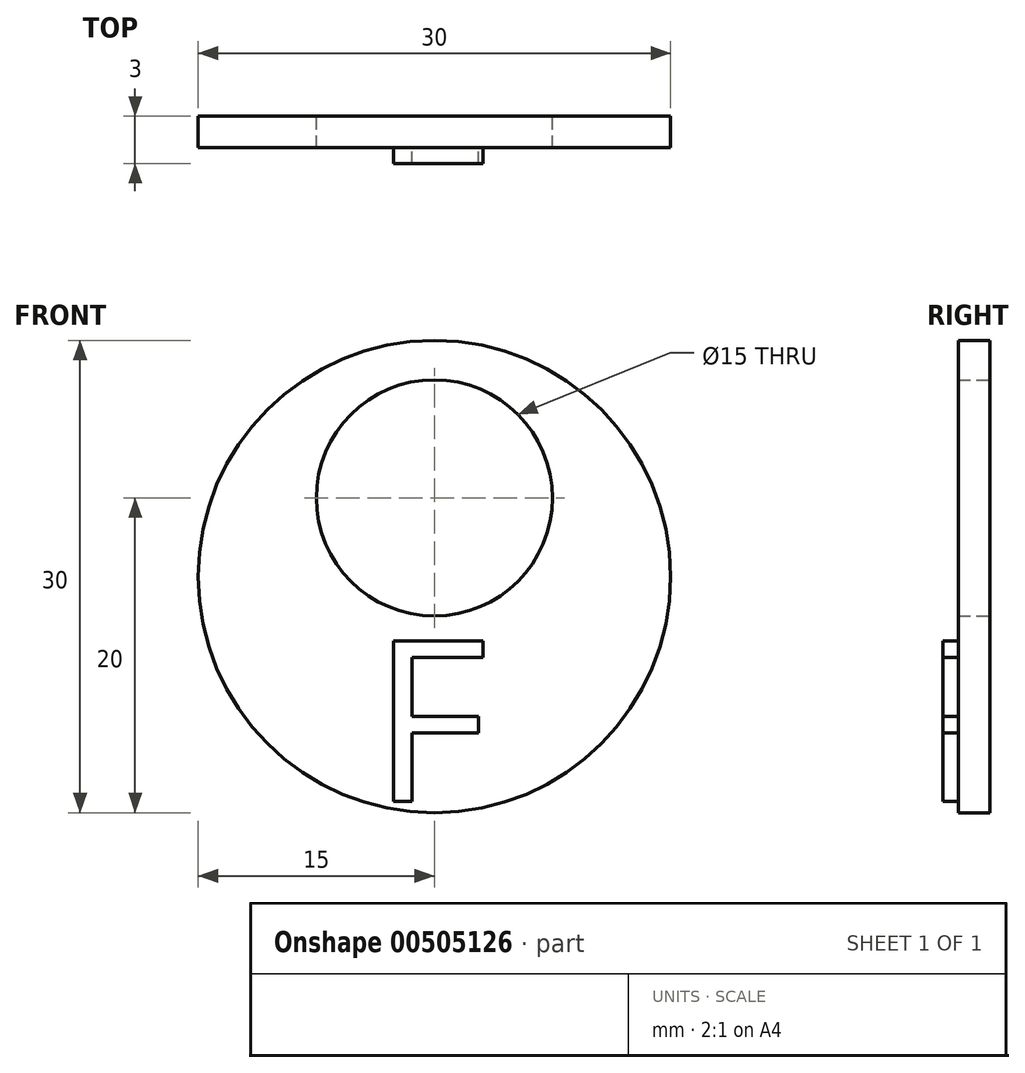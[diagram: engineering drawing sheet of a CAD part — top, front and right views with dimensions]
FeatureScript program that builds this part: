
annotation { "Feature Type Name" : "Feature", "Feature Type Description" : "" }
export const myFeature = defineFeature(function(context is Context, id is Id, definition is map)
    precondition{}
    {
        {
            var Q0;
            Q0=qCreatedBy(makeId("Front.planeOp"),FACE);
            var sketch = newSketch(context, id + "F0", { "sketchPlane" : qUnion([Q0])});
            skCircle(sketch, "E0", {"center": v(0, 0) * mm, "radius": 15 * mm});
            skPoint(sketch, "E1", {"position": v(0, 5) * mm});
            skCircle(sketch, "E2", {"center": v(0, 5) * mm, "radius": 7.5 * mm});
            skSolve(sketch);
        }
        {
            var Q0;
            Q0=makeQuery(id+"F0.imprint","IMPRINT",FACE,{"disambiguationData":[TD([[makeQuery(id+"F0.imprint","IMPRINT",EDGE,{"derivedFrom":sQuery(id+"F0.wireOp",EDGE,"E0")}),1.0]])]});
            extrude(context, id + "F1", {"entities" : qUnion([Q0]), "depth" : 2 * mm});
        }
        {
            var Q0;
            Q0=makeQuery(id+"F1.opExtrude","CAP_FACE",FACE,{"disambiguationData":[OSD([sQuery(id+"F0.wireOp",EDGE,"E0"),sQuery(id+"F0.wireOp",EDGE,"E2")])],"isStart":false});
            var sketch = newSketch(context, id + "F2", { "sketchPlane" : qUnion([Q0])});
            skText(sketch, "E3", { "text": "F", "fontName": "OpenSans-Regular.ttf"});
            const initialGuessF2  = {"E3": [-0.004, -0.01427, 1, 0, 0.01027]};
            skSetInitialGuess(sketch, initialGuessF2);
            skSolve(sketch);
        }
        {
            var Q0;
            Q0=qSketchRegion(id+"F2",true);
            extrude(context, id + "F3", {"entities" : qUnion([Q0]), "operationType" : NewBodyOperationType.ADD, "depth" : 1 * mm});
        }
    });
